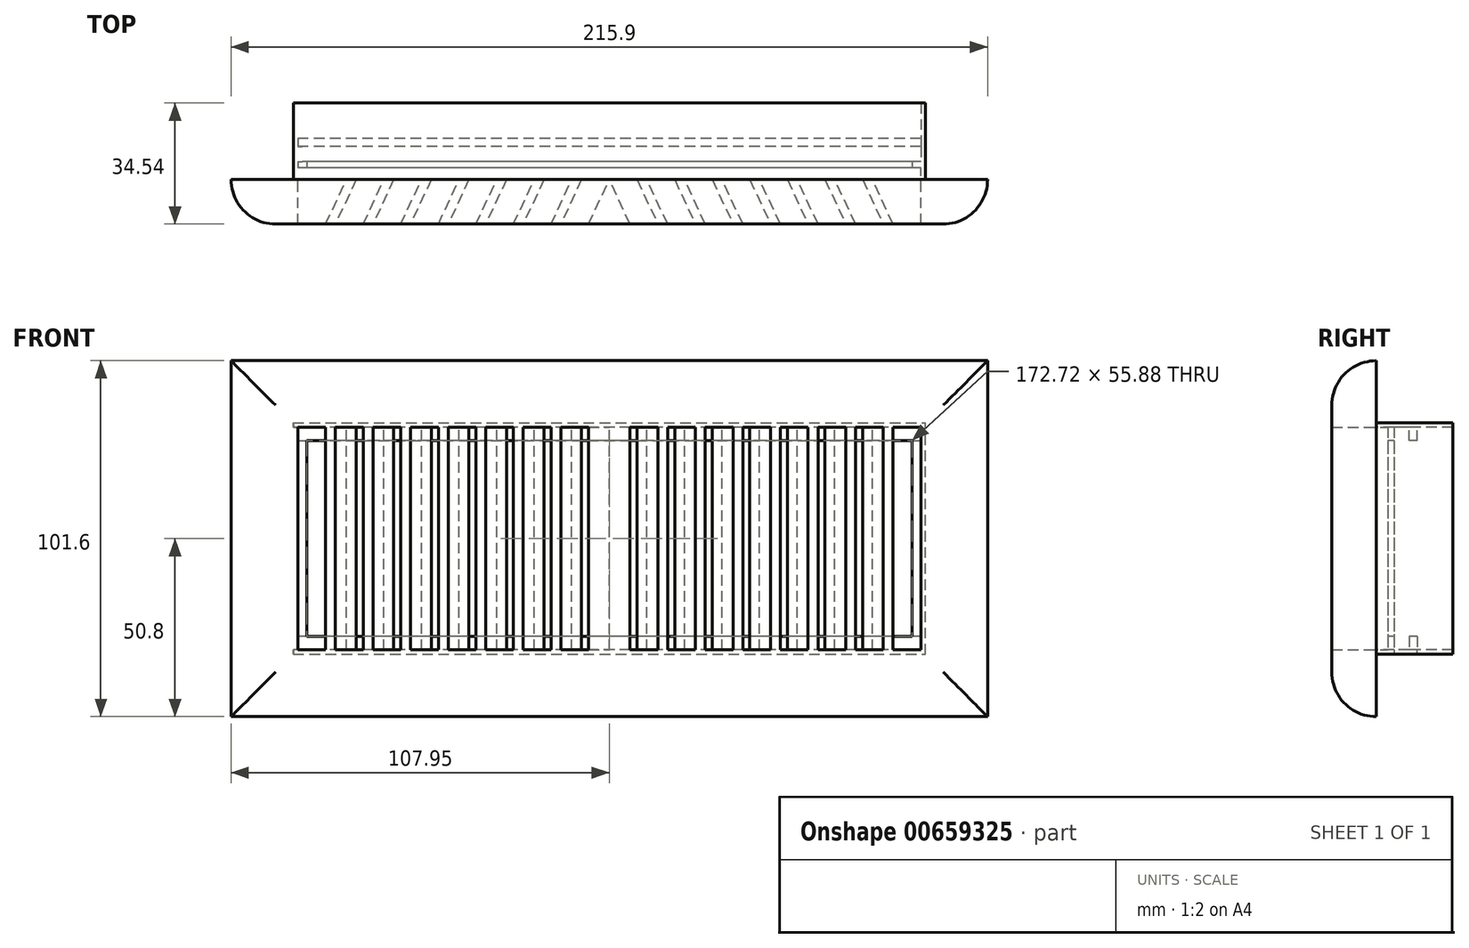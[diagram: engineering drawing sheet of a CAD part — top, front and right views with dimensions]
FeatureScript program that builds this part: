
annotation { "Feature Type Name" : "Feature", "Feature Type Description" : "" }
export const myFeature = defineFeature(function(context is Context, id is Id, definition is map)
    precondition{}
    {
        {
            var Q0;
            Q0=qCreatedBy(makeId("Front.planeOp"),FACE);
            var sketch = newSketch(context, id + "F0", { "sketchPlane" : qUnion([Q0])});
            skLineSegment(sketch, "E0.bottom", {"start": v(107.95, -50.8) * mm, "end": v(-107.95, -50.8) * mm});
            skLineSegment(sketch, "E0.top", {"start": v(107.95, 50.8) * mm, "end": v(-107.95, 50.8) * mm});
            skLineSegment(sketch, "E0.left", {"start": v(107.95, -50.8) * mm, "end": v(107.95, 50.8) * mm});
            skLineSegment(sketch, "E0.right", {"start": v(-107.95, -50.8) * mm, "end": v(-107.95, 50.8) * mm});
            skPoint(sketch, "E0.middle", {"position": v(0, 0) * mm});
            skLineSegment(sketch, "E1.bottom", {"start": v(88.9, -31.75) * mm, "end": v(-88.9, -31.75) * mm});
            skLineSegment(sketch, "E1.top", {"start": v(88.9, 31.75) * mm, "end": v(-88.9, 31.75) * mm});
            skLineSegment(sketch, "E1.left", {"start": v(88.9, -31.75) * mm, "end": v(88.9, 31.75) * mm});
            skLineSegment(sketch, "E1.right", {"start": v(-88.9, -31.75) * mm, "end": v(-88.9, 31.75) * mm});
            skSolve(sketch);
        }
        {
            var Q0;
            Q0=makeQuery(id+"F0.imprint","IMPRINT",FACE,{"disambiguationData":[TD([[makeQuery(id+"F0.imprint","IMPRINT",EDGE,{"derivedFrom":sQuery(id+"F0.wireOp",EDGE,"E0.bottom")}),-1.0]])]});
            extrude(context, id + "F1", {"entities" : qUnion([Q0]), "depth" : 12.7 * mm});
        }
        {
            var Q0;
            Q0=makeQuery(id+"F1.opExtrude","SWEPT_FACE",FACE,{"disambiguationData":[OSD([sQuery(id+"F0.wireOp",EDGE,"E0.top")])]});
            var sketch = newSketch(context, id + "F2", { "sketchPlane" : qUnion([Q0])});
            skLineSegment(sketch, "E2", {"start": v(-75.05, 0) * mm, "end": v(-80.97, -12.7) * mm});
            skLineSegment(sketch, "E3", {"start": v(-80.97, -12.7) * mm, "end": v(-78.17, -12.7) * mm});
            skLineSegment(sketch, "E4", {"start": v(-78.17, -12.7) * mm, "end": v(-72.25, 0) * mm});
            skLineSegment(sketch, "E5", {"start": v(-72.25, 0) * mm, "end": v(-75.05, 0) * mm});
            skLineSegment(sketch, "E6.1.0.0", {"start": v(-64.33, 0) * mm, "end": v(-70.25, -12.7) * mm});
            skLineSegment(sketch, "E6.1.0.1", {"start": v(-70.25, -12.7) * mm, "end": v(-67.45, -12.7) * mm});
            skLineSegment(sketch, "E6.1.0.2", {"start": v(-67.45, -12.7) * mm, "end": v(-61.53, 0) * mm});
            skLineSegment(sketch, "E6.1.0.3", {"start": v(-61.53, 0) * mm, "end": v(-64.33, 0) * mm});
            skLineSegment(sketch, "E6.2.0.0", {"start": v(-53.6, 0) * mm, "end": v(-59.53, -12.7) * mm});
            skLineSegment(sketch, "E6.2.0.1", {"start": v(-59.53, -12.7) * mm, "end": v(-56.73, -12.7) * mm});
            skLineSegment(sketch, "E6.2.0.2", {"start": v(-56.73, -12.7) * mm, "end": v(-50.8, 0) * mm});
            skLineSegment(sketch, "E6.2.0.3", {"start": v(-50.8, 0) * mm, "end": v(-53.6, 0) * mm});
            skLineSegment(sketch, "E6.3.0.0", {"start": v(-42.88, 0) * mm, "end": v(-48.8, -12.7) * mm});
            skLineSegment(sketch, "E6.3.0.1", {"start": v(-48.8, -12.7) * mm, "end": v(-46, -12.7) * mm});
            skLineSegment(sketch, "E6.3.0.2", {"start": v(-46, -12.7) * mm, "end": v(-40.08, 0) * mm});
            skLineSegment(sketch, "E6.3.0.3", {"start": v(-40.08, 0) * mm, "end": v(-42.88, 0) * mm});
            skLineSegment(sketch, "E6.4.0.0", {"start": v(-32.16, 0) * mm, "end": v(-38.08, -12.7) * mm});
            skLineSegment(sketch, "E6.4.0.1", {"start": v(-38.08, -12.7) * mm, "end": v(-35.28, -12.7) * mm});
            skLineSegment(sketch, "E6.4.0.2", {"start": v(-35.28, -12.7) * mm, "end": v(-29.36, 0) * mm});
            skLineSegment(sketch, "E6.4.0.3", {"start": v(-29.36, 0) * mm, "end": v(-32.16, 0) * mm});
            skLineSegment(sketch, "E6.5.0.0", {"start": v(-21.44, 0) * mm, "end": v(-27.36, -12.7) * mm});
            skLineSegment(sketch, "E6.5.0.1", {"start": v(-27.36, -12.7) * mm, "end": v(-24.56, -12.7) * mm});
            skLineSegment(sketch, "E6.5.0.2", {"start": v(-24.56, -12.7) * mm, "end": v(-18.64, 0) * mm});
            skLineSegment(sketch, "E6.5.0.3", {"start": v(-18.64, 0) * mm, "end": v(-21.44, 0) * mm});
            skLineSegment(sketch, "E6.6.0.0", {"start": v(-10.72, 0) * mm, "end": v(-16.64, -12.7) * mm});
            skLineSegment(sketch, "E6.6.0.1", {"start": v(-16.64, -12.7) * mm, "end": v(-13.84, -12.7) * mm});
            skLineSegment(sketch, "E6.6.0.2", {"start": v(-13.84, -12.7) * mm, "end": v(-7.92, 0) * mm});
            skLineSegment(sketch, "E6.6.0.3", {"start": v(-7.92, 0) * mm, "end": v(-10.72, 0) * mm});
            skLineSegment(sketch, "E6.direction1", {"start": v(-80.97, -12.7) * mm, "end": v(-70.25, -12.7) * mm, "construction": true});
            skLineSegment(sketch, "E7", {"start": v(75.05, 0) * mm, "end": v(80.97, -12.7) * mm});
            skLineSegment(sketch, "E8", {"start": v(80.97, -12.7) * mm, "end": v(78.17, -12.7) * mm});
            skLineSegment(sketch, "E9", {"start": v(78.17, -12.7) * mm, "end": v(72.25, 0) * mm});
            skLineSegment(sketch, "E10", {"start": v(72.25, 0) * mm, "end": v(75.05, 0) * mm});
            skLineSegment(sketch, "E11.1.0.0", {"start": v(70.25, -12.7) * mm, "end": v(67.45, -12.7) * mm});
            skLineSegment(sketch, "E11.1.0.1", {"start": v(64.33, 0) * mm, "end": v(70.25, -12.7) * mm});
            skLineSegment(sketch, "E11.1.0.2", {"start": v(61.53, 0) * mm, "end": v(64.33, 0) * mm});
            skLineSegment(sketch, "E11.1.0.3", {"start": v(67.45, -12.7) * mm, "end": v(61.53, 0) * mm});
            skLineSegment(sketch, "E11.2.0.0", {"start": v(59.53, -12.7) * mm, "end": v(56.73, -12.7) * mm});
            skLineSegment(sketch, "E11.2.0.1", {"start": v(53.6, 0) * mm, "end": v(59.53, -12.7) * mm});
            skLineSegment(sketch, "E11.2.0.2", {"start": v(50.8, 0) * mm, "end": v(53.6, 0) * mm});
            skLineSegment(sketch, "E11.2.0.3", {"start": v(56.73, -12.7) * mm, "end": v(50.8, 0) * mm});
            skLineSegment(sketch, "E11.3.0.0", {"start": v(48.8, -12.7) * mm, "end": v(46, -12.7) * mm});
            skLineSegment(sketch, "E11.3.0.1", {"start": v(42.88, 0) * mm, "end": v(48.8, -12.7) * mm});
            skLineSegment(sketch, "E11.3.0.2", {"start": v(40.08, 0) * mm, "end": v(42.88, 0) * mm});
            skLineSegment(sketch, "E11.3.0.3", {"start": v(46, -12.7) * mm, "end": v(40.08, 0) * mm});
            skLineSegment(sketch, "E11.4.0.0", {"start": v(38.08, -12.7) * mm, "end": v(35.28, -12.7) * mm});
            skLineSegment(sketch, "E11.4.0.1", {"start": v(32.16, 0) * mm, "end": v(38.08, -12.7) * mm});
            skLineSegment(sketch, "E11.4.0.2", {"start": v(29.36, 0) * mm, "end": v(32.16, 0) * mm});
            skLineSegment(sketch, "E11.4.0.3", {"start": v(35.28, -12.7) * mm, "end": v(29.36, 0) * mm});
            skLineSegment(sketch, "E11.5.0.0", {"start": v(27.36, -12.7) * mm, "end": v(24.56, -12.7) * mm});
            skLineSegment(sketch, "E11.5.0.1", {"start": v(21.44, 0) * mm, "end": v(27.36, -12.7) * mm});
            skLineSegment(sketch, "E11.5.0.2", {"start": v(18.64, 0) * mm, "end": v(21.44, 0) * mm});
            skLineSegment(sketch, "E11.5.0.3", {"start": v(24.56, -12.7) * mm, "end": v(18.64, 0) * mm});
            skLineSegment(sketch, "E11.6.0.0", {"start": v(16.64, -12.7) * mm, "end": v(13.84, -12.7) * mm});
            skLineSegment(sketch, "E11.6.0.1", {"start": v(10.72, 0) * mm, "end": v(16.64, -12.7) * mm});
            skLineSegment(sketch, "E11.6.0.2", {"start": v(7.92, 0) * mm, "end": v(10.72, 0) * mm});
            skLineSegment(sketch, "E11.6.0.3", {"start": v(13.84, -12.7) * mm, "end": v(7.92, 0) * mm});
            skLineSegment(sketch, "E11.direction1", {"start": v(78.17, -12.7) * mm, "end": v(67.45, -12.7) * mm, "construction": true});
            skLineSegment(sketch, "E12", {"start": v(0, 0) * mm, "end": v(0, -12.7) * mm, "construction": true});
            skLineSegment(sketch, "E13", {"start": v(0, 0) * mm, "end": v(-5.92, -12.7) * mm});
            skLineSegment(sketch, "E14", {"start": v(0, 0) * mm, "end": v(5.92, -12.7) * mm});
            skLineSegment(sketch, "E15", {"start": v(-5.92, -12.7) * mm, "end": v(5.92, -12.7) * mm});
            skSolve(sketch);
        }
        {
            var Q0;
            Q0=qSketchRegion(id+"F2",true);
            extrude(context, id + "F3", {"entities" : qUnion([Q0]), "operationType" : NewBodyOperationType.ADD, "oppositeDirection" : true, "depth" : 101.6 * mm});
        }
        {
            var Q0;
            Q0=makeQuery(id+"F1.opExtrude","CAP_EDGE",EDGE,{"disambiguationData":[OSD([sQuery(id+"F0.wireOp",EDGE,"E0.top")])],"isStart":false});
            var Q1;
            Q1=makeQuery(id+"F1.opExtrude","CAP_EDGE",EDGE,{"disambiguationData":[OSD([sQuery(id+"F0.wireOp",EDGE,"E0.right")])],"isStart":false});
            var Q2;
            Q2=makeQuery(id+"F1.opExtrude","CAP_EDGE",EDGE,{"disambiguationData":[OSD([sQuery(id+"F0.wireOp",EDGE,"E0.bottom")])],"isStart":false});
            var Q3;
            Q3=makeQuery(id+"F1.opExtrude","CAP_EDGE",EDGE,{"disambiguationData":[OSD([sQuery(id+"F0.wireOp",EDGE,"E0.left")])],"isStart":false});
            fillet(context, id + "F4", {"entities" : qUnion([Q0, Q1, Q2, Q3]), "radius" : 12.7 * mm, "tangentPropagation" : true, "allowEdgeOverflow" : false});
        }
        {
            var Q0;
            Q0=makeQuery(id+"F3.boolean.opBoolean","MERGE",FACE,{"derivedFrom":[makeQuery(id+"F1.opExtrude","CAP_FACE",FACE,{"disambiguationData":[OSD([sQuery(id+"F0.wireOp",EDGE,"E0.bottom"),sQuery(id+"F0.wireOp",EDGE,"E0.top"),sQuery(id+"F0.wireOp",EDGE,"E0.left"),sQuery(id+"F0.wireOp",EDGE,"E0.right"),sQuery(id+"F0.wireOp",EDGE,"E1.bottom"),sQuery(id+"F0.wireOp",EDGE,"E1.top"),sQuery(id+"F0.wireOp",EDGE,"E1.left"),sQuery(id+"F0.wireOp",EDGE,"E1.right")])],"isStart":true}),makeQuery(id+"F3.opExtrude","SWEPT_FACE",FACE,{"disambiguationData":[OSD([sQuery(id+"F2.wireOp",EDGE,"E5")])]}),makeQuery(id+"F3.opExtrude","SWEPT_FACE",FACE,{"disambiguationData":[OSD([sQuery(id+"F2.wireOp",EDGE,"E6.1.0.3")])]}),makeQuery(id+"F3.opExtrude","SWEPT_FACE",FACE,{"disambiguationData":[OSD([sQuery(id+"F2.wireOp",EDGE,"E6.2.0.3")])]}),makeQuery(id+"F3.opExtrude","SWEPT_FACE",FACE,{"disambiguationData":[OSD([sQuery(id+"F2.wireOp",EDGE,"E6.3.0.3")])]}),makeQuery(id+"F3.opExtrude","SWEPT_FACE",FACE,{"disambiguationData":[OSD([sQuery(id+"F2.wireOp",EDGE,"E6.4.0.3")])]}),makeQuery(id+"F3.opExtrude","SWEPT_FACE",FACE,{"disambiguationData":[OSD([sQuery(id+"F2.wireOp",EDGE,"E6.5.0.3")])]}),makeQuery(id+"F3.opExtrude","SWEPT_FACE",FACE,{"disambiguationData":[OSD([sQuery(id+"F2.wireOp",EDGE,"E6.6.0.3")])]}),makeQuery(id+"F3.opExtrude","SWEPT_FACE",FACE,{"disambiguationData":[OSD([sQuery(id+"F2.wireOp",EDGE,"E10")])]}),makeQuery(id+"F3.opExtrude","SWEPT_FACE",FACE,{"disambiguationData":[OSD([sQuery(id+"F2.wireOp",EDGE,"E11.1.0.2")])]}),makeQuery(id+"F3.opExtrude","SWEPT_FACE",FACE,{"disambiguationData":[OSD([sQuery(id+"F2.wireOp",EDGE,"E11.2.0.2")])]}),makeQuery(id+"F3.opExtrude","SWEPT_FACE",FACE,{"disambiguationData":[OSD([sQuery(id+"F2.wireOp",EDGE,"E11.3.0.2")])]}),makeQuery(id+"F3.opExtrude","SWEPT_FACE",FACE,{"disambiguationData":[OSD([sQuery(id+"F2.wireOp",EDGE,"E11.4.0.2")])]}),makeQuery(id+"F3.opExtrude","SWEPT_FACE",FACE,{"disambiguationData":[OSD([sQuery(id+"F2.wireOp",EDGE,"E11.5.0.2")])]}),makeQuery(id+"F3.opExtrude","SWEPT_FACE",FACE,{"disambiguationData":[OSD([sQuery(id+"F2.wireOp",EDGE,"E11.6.0.2")])]})]});
            var sketch = newSketch(context, id + "F5", { "sketchPlane" : qUnion([Q0])});
            skLineSegment(sketch, "E16.bottom", {"start": v(90.17, -33.02) * mm, "end": v(-90.17, -33.02) * mm});
            skLineSegment(sketch, "E16.top", {"start": v(90.17, 33.02) * mm, "end": v(-90.17, 33.02) * mm});
            skLineSegment(sketch, "E16.right", {"start": v(-90.17, -33.02) * mm, "end": v(-90.17, 33.02) * mm});
            skPoint(sketch, "E16.middle", {"position": v(0, 0) * mm});
            skLineSegment(sketch, "E17.bottom", {"start": v(88.9, -31.75) * mm, "end": v(-88.9, -31.75) * mm});
            skLineSegment(sketch, "E17.top", {"start": v(88.9, 31.75) * mm, "end": v(-88.9, 31.75) * mm});
            skLineSegment(sketch, "E17.right", {"start": v(-88.9, -31.75) * mm, "end": v(-88.9, 31.75) * mm});
            skLineSegment(sketch, "E18", {"start": v(88.9, 31.75) * mm, "end": v(90.17, 31.75) * mm});
            skLineSegment(sketch, "E19", {"start": v(90.17, 31.75) * mm, "end": v(90.17, 33.02) * mm});
            skLineSegment(sketch, "E20", {"start": v(88.9, -31.75) * mm, "end": v(90.17, -31.75) * mm});
            skLineSegment(sketch, "E21", {"start": v(90.17, -31.75) * mm, "end": v(90.17, -33.02) * mm});
            skSolve(sketch);
        }
        {
            var Q0;
            Q0=qSketchRegion(id+"F5",true);
            extrude(context, id + "F6", {"entities" : qUnion([Q0]), "operationType" : NewBodyOperationType.ADD, "depth" : 3.3 * mm});
        }
        {
            var Q0;
            Q0=makeQuery(id+"F6.opExtrude","CAP_FACE",FACE,{"disambiguationData":[OSD([sQuery(id+"F5.wireOp",EDGE,"E16.bottom"),sQuery(id+"F5.wireOp",EDGE,"E16.top"),sQuery(id+"F5.wireOp",EDGE,"E16.right"),sQuery(id+"F5.wireOp",EDGE,"E17.bottom"),sQuery(id+"F5.wireOp",EDGE,"E17.top"),sQuery(id+"F5.wireOp",EDGE,"E17.right"),sQuery(id+"F5.wireOp",EDGE,"E18"),sQuery(id+"F5.wireOp",EDGE,"E19"),sQuery(id+"F5.wireOp",EDGE,"E20"),sQuery(id+"F5.wireOp",EDGE,"E21")])],"isStart":false});
            var sketch = newSketch(context, id + "F7", { "sketchPlane" : qUnion([Q0])});
            skLineSegment(sketch, "E22.bottom", {"start": v(-90.17, 33.02) * mm, "end": v(88.9, 33.02) * mm});
            skLineSegment(sketch, "E22.top", {"start": v(-90.17, -33.02) * mm, "end": v(88.9, -33.02) * mm});
            skLineSegment(sketch, "E22.left", {"start": v(-90.17, 33.02) * mm, "end": v(-90.17, -33.02) * mm});
            skLineSegment(sketch, "E22.right", {"start": v(88.9, 33.02) * mm, "end": v(88.9, -33.02) * mm});
            skLineSegment(sketch, "E23.bottom", {"start": v(-86.36, 27.94) * mm, "end": v(86.36, 27.94) * mm});
            skLineSegment(sketch, "E23.top", {"start": v(-86.36, -27.94) * mm, "end": v(86.36, -27.94) * mm});
            skLineSegment(sketch, "E23.left", {"start": v(-86.36, 27.94) * mm, "end": v(-86.36, -27.94) * mm});
            skLineSegment(sketch, "E23.right", {"start": v(86.36, 27.94) * mm, "end": v(86.36, -27.94) * mm});
            skSolve(sketch);
        }
        {
            var Q0;
            Q0=qSketchRegion(id+"F7",true);
            extrude(context, id + "F8", {"entities" : qUnion([Q0]), "operationType" : NewBodyOperationType.ADD, "depth" : 1.78 * mm});
        }
        {
            var Q0;
            Q0=makeQuery(id+"F8.opExtrude","CAP_FACE",FACE,{"disambiguationData":[OSD([sQuery(id+"F7.wireOp",EDGE,"E22.bottom"),sQuery(id+"F7.wireOp",EDGE,"E22.top"),sQuery(id+"F7.wireOp",EDGE,"E22.left"),sQuery(id+"F7.wireOp",EDGE,"E22.right"),sQuery(id+"F7.wireOp",EDGE,"E23.bottom"),sQuery(id+"F7.wireOp",EDGE,"E23.top"),sQuery(id+"F7.wireOp",EDGE,"E23.left"),sQuery(id+"F7.wireOp",EDGE,"E23.right")])],"isStart":false});
            var sketch = newSketch(context, id + "F9", { "sketchPlane" : qUnion([Q0])});
            skLineSegment(sketch, "E24.bottom", {"start": v(-90.17, 33.02) * mm, "end": v(88.9, 33.02) * mm});
            skLineSegment(sketch, "E24.top", {"start": v(-90.17, -33.02) * mm, "end": v(88.9, -33.02) * mm});
            skLineSegment(sketch, "E24.left", {"start": v(-90.17, 33.02) * mm, "end": v(-90.17, -33.02) * mm});
            skLineSegment(sketch, "E25.bottom", {"start": v(-88.9, 31.75) * mm, "end": v(87.63, 31.75) * mm});
            skLineSegment(sketch, "E25.top", {"start": v(-88.9, -31.75) * mm, "end": v(87.63, -31.75) * mm});
            skLineSegment(sketch, "E25.left", {"start": v(-88.9, 31.75) * mm, "end": v(-88.9, -31.75) * mm});
            skLineSegment(sketch, "E26", {"start": v(88.9, -33.02) * mm, "end": v(90.18, -33.02) * mm});
            skLineSegment(sketch, "E27", {"start": v(90.18, -33.02) * mm, "end": v(90.18, -31.75) * mm});
            skLineSegment(sketch, "E28", {"start": v(90.18, -31.75) * mm, "end": v(87.63, -31.75) * mm});
            skLineSegment(sketch, "E29", {"start": v(88.9, 33.02) * mm, "end": v(90.17, 33.02) * mm});
            skLineSegment(sketch, "E30", {"start": v(90.17, 33.02) * mm, "end": v(90.17, 31.75) * mm});
            skLineSegment(sketch, "E31", {"start": v(90.17, 31.75) * mm, "end": v(87.63, 31.75) * mm});
            skSolve(sketch);
        }
        {
            var Q0;
            {var subQ5=sQuery(id+"F9.wireOp",EDGE,"E24.bottom");Q0=makeQuery(id+"F9.imprint","IMPRINT",FACE,{"disambiguationData":[TD([[makeQuery(id+"F9.imprint","IMPRINT",EDGE,{"derivedFrom":subQ5}),1.0]])]});}
            var Q1;
            {var subQ0=sQuery(id+"F9.wireOp",EDGE,"E29");Q1=makeQuery(id+"F9.imprint","IMPRINT",FACE,{"disambiguationData":[TD([[makeQuery(id+"F9.imprint","IMPRINT",EDGE,{"derivedFrom":subQ0}),-1.0]])]});}
            var Q2;
            {var subQ0=sQuery(id+"F9.wireOp",EDGE,"E26");Q2=makeQuery(id+"F9.imprint","IMPRINT",FACE,{"disambiguationData":[TD([[makeQuery(id+"F9.imprint","IMPRINT",EDGE,{"derivedFrom":subQ0}),1.0]])]});}
            extrude(context, id + "F10", {"entities" : qUnion([Q0, Q1, Q2]), "operationType" : NewBodyOperationType.ADD, "depth" : 4.32 * mm});
        }
        {
            var Q0;
            {var subQ0=sQuery(id+"F5.wireOp",EDGE,"E21");var subQ1=sQuery(id+"F5.wireOp",EDGE,"E20");var subQ2=sQuery(id+"F5.wireOp",EDGE,"E17.bottom");var subQ3=sQuery(id+"F5.wireOp",EDGE,"E16.bottom");Q0=makeQuery(id+"F8.boolean.opBoolean","SPLIT",FACE,{"disambiguationData":[TD([makeQuery(id+"F1.opExtrude","SWEPT_FACE",FACE,{"disambiguationData":[OSD([sQuery(id+"F0.wireOp",EDGE,"E1.bottom")])]})])],"derivedFrom":makeQuery(id+"F6.opExtrude","CAP_FACE",FACE,{"disambiguationData":[OSD([subQ3,sQuery(id+"F5.wireOp",EDGE,"E16.top"),sQuery(id+"F5.wireOp",EDGE,"E16.right"),subQ2,sQuery(id+"F5.wireOp",EDGE,"E17.top"),sQuery(id+"F5.wireOp",EDGE,"E17.right"),sQuery(id+"F5.wireOp",EDGE,"E18"),sQuery(id+"F5.wireOp",EDGE,"E19"),subQ1,subQ0])],"isStart":false})});}
            var sketch = newSketch(context, id + "F11", { "sketchPlane" : qUnion([Q0])});
            skLineSegment(sketch, "E32.bottom", {"start": v(88.9, -33.02) * mm, "end": v(90.17, -33.02) * mm});
            skLineSegment(sketch, "E32.top", {"start": v(88.9, -31.75) * mm, "end": v(90.17, -31.75) * mm});
            skLineSegment(sketch, "E32.left", {"start": v(88.9, -33.02) * mm, "end": v(88.9, -31.75) * mm});
            skLineSegment(sketch, "E32.right", {"start": v(90.17, -33.02) * mm, "end": v(90.17, -31.75) * mm});
            skSolve(sketch);
        }
        {
            var Q0;
            Q0=qSketchRegion(id+"F11",true);
            extrude(context, id + "F12", {"entities" : qUnion([Q0]), "operationType" : NewBodyOperationType.ADD, "depth" : 1.78 * mm});
        }
        {
            var Q0;
            Q0=makeQuery(id+"F10.opExtrude","CAP_FACE",FACE,{"disambiguationData":[OSD([sQuery(id+"F9.wireOp",EDGE,"E24.bottom"),sQuery(id+"F9.wireOp",EDGE,"E24.top"),sQuery(id+"F9.wireOp",EDGE,"E24.left"),sQuery(id+"F9.wireOp",EDGE,"E25.bottom"),sQuery(id+"F9.wireOp",EDGE,"E25.top"),sQuery(id+"F9.wireOp",EDGE,"E25.left"),sQuery(id+"F9.wireOp",EDGE,"E26"),sQuery(id+"F9.wireOp",EDGE,"E27"),sQuery(id+"F9.wireOp",EDGE,"E28"),sQuery(id+"F9.wireOp",EDGE,"E29"),sQuery(id+"F9.wireOp",EDGE,"E30"),sQuery(id+"F9.wireOp",EDGE,"E31")])],"isStart":false});
            var sketch = newSketch(context, id + "F13", { "sketchPlane" : qUnion([Q0])});
            skLineSegment(sketch, "E33.bottom", {"start": v(-90.17, 33.02) * mm, "end": v(88.9, 33.02) * mm});
            skLineSegment(sketch, "E33.top", {"start": v(-90.17, -33.02) * mm, "end": v(88.9, -33.02) * mm});
            skLineSegment(sketch, "E34.bottom", {"start": v(-84.84, 27.94) * mm, "end": v(88.9, 27.94) * mm});
            skLineSegment(sketch, "E34.top", {"start": v(-84.84, -27.94) * mm, "end": v(88.9, -27.94) * mm});
            skLineSegment(sketch, "E35", {"start": v(-84.84, 27.94) * mm, "end": v(-90.17, 27.94) * mm});
            skLineSegment(sketch, "E36", {"start": v(-90.17, 27.94) * mm, "end": v(-90.17, 33.02) * mm});
            skLineSegment(sketch, "E37", {"start": v(-84.84, -27.94) * mm, "end": v(-90.17, -27.94) * mm});
            skLineSegment(sketch, "E38", {"start": v(-90.17, -27.94) * mm, "end": v(-90.17, -33.02) * mm});
            skLineSegment(sketch, "E39.bottom", {"start": v(-90.17, 27.94) * mm, "end": v(-88.9, 27.94) * mm});
            skLineSegment(sketch, "E39.top", {"start": v(-90.17, -27.94) * mm, "end": v(-88.9, -27.94) * mm});
            skLineSegment(sketch, "E39.left", {"start": v(-90.17, 27.94) * mm, "end": v(-90.17, -27.94) * mm});
            skLineSegment(sketch, "E39.right", {"start": v(-88.9, 27.94) * mm, "end": v(-88.9, -27.94) * mm});
            skLineSegment(sketch, "E40", {"start": v(88.9, -27.94) * mm, "end": v(88.9, -33.02) * mm});
            skLineSegment(sketch, "E41", {"start": v(88.9, 27.94) * mm, "end": v(88.9, 33.02) * mm});
            skSolve(sketch);
        }
        {
            var Q0;
            Q0=qSketchRegion(id+"F13",true);
            extrude(context, id + "F14", {"entities" : qUnion([Q0]), "operationType" : NewBodyOperationType.ADD, "depth" : 2.3 * mm});
        }
        {
            var Q0;
            Q0=makeQuery(id+"F14.opExtrude","SWEPT_FACE",FACE,{"disambiguationData":[OSD([sQuery(id+"F13.wireOp",EDGE,"E34.top"),sQuery(id+"F13.wireOp",EDGE,"E37"),sQuery(id+"F13.wireOp",EDGE,"TGxW7JvE-hO0u-tt39-ioUT-bYuH0o1wrKsi")])]});
            var sketch = newSketch(context, id + "F15", { "sketchPlane" : qUnion([Q0])});
            skSolve(sketch);
        }
        {
            var Q0;
            Q0=makeQuery(id+"Fv8F5Soem3vfvmW_1.boolean.opBoolean","MERGE",FACE,{"derivedFrom":[makeQuery(id+"F14.opExtrude","CAP_FACE",FACE,{"disambiguationData":[OSD([sQuery(id+"F13.wireOp",EDGE,"E33.bottom"),sQuery(id+"F13.wireOp",EDGE,"E33.top"),sQuery(id+"F13.wireOp",EDGE,"E34.bottom"),sQuery(id+"F13.wireOp",EDGE,"E34.top"),sQuery(id+"F13.wireOp",EDGE,"E35"),sQuery(id+"F13.wireOp",EDGE,"E36"),sQuery(id+"F13.wireOp",EDGE,"E37"),sQuery(id+"F13.wireOp",EDGE,"E38"),sQuery(id+"F13.wireOp",EDGE,"E39.left"),sQuery(id+"F13.wireOp",EDGE,"E39.right"),sQuery(id+"F13.wireOp",EDGE,"TGxW7JvE-hO0u-tt39-ioUT-bYuH0o1wrKsi"),sQuery(id+"F13.wireOp",EDGE,"xJwFBrmR-DKHQ-Ms6E-cGLF-1sDl0en4KIHk"),sQuery(id+"F13.wireOp",EDGE,"KjPjYPhn-M9NA-BWyU-6eae-7lh8KEkwCyoe"),sQuery(id+"F13.wireOp",EDGE,"DDPbrne3-7nOW-QVff-d2O1-u6GeuogKL0BI")])],"isStart":false}),makeQuery(id+"Fv8F5Soem3vfvmW_1.opExtrude","SWEPT_FACE",FACE,{"disambiguationData":[OSD([sQuery(id+"F15.wireOp",EDGE,"I5fvG48v-rP8C-mtnB-2jEv-sWBCkAZKz6mY.bottom")])]})]});
            var sketch = newSketch(context, id + "F16", { "sketchPlane" : qUnion([Q0])});
            skLineSegment(sketch, "E42.bottom", {"start": v(-90.17, 33.02) * mm, "end": v(90.17, 33.02) * mm});
            skLineSegment(sketch, "E42.top", {"start": v(-90.17, -33.02) * mm, "end": v(90.17, -33.02) * mm});
            skLineSegment(sketch, "E42.left", {"start": v(-90.17, 33.02) * mm, "end": v(-90.17, -33.02) * mm});
            skLineSegment(sketch, "E43.bottom", {"start": v(-88.9, 31.75) * mm, "end": v(84.62, 31.75) * mm});
            skLineSegment(sketch, "E43.top", {"start": v(-88.9, -31.75) * mm, "end": v(84.62, -31.75) * mm});
            skLineSegment(sketch, "E43.left", {"start": v(-88.9, 31.75) * mm, "end": v(-88.9, -31.75) * mm});
            skLineSegment(sketch, "E44", {"start": v(84.62, 31.75) * mm, "end": v(90.17, 31.75) * mm});
            skLineSegment(sketch, "E45", {"start": v(90.17, 33.02) * mm, "end": v(90.17, 31.75) * mm});
            skLineSegment(sketch, "E46", {"start": v(84.62, -31.75) * mm, "end": v(90.17, -31.75) * mm});
            skLineSegment(sketch, "E47", {"start": v(90.17, -33.02) * mm, "end": v(90.17, -31.75) * mm});
            skSolve(sketch);
        }
        {
            var Q0;
            Q0=qSketchRegion(id+"F16",true);
            extrude(context, id + "F17", {"entities" : qUnion([Q0]), "operationType" : NewBodyOperationType.ADD, "depth" : 10.16 * mm});
        }
        {
            var Q0;
            {var subQ0=sQuery(id+"F5.wireOp",EDGE,"E18");var subQ1=sQuery(id+"F5.wireOp",EDGE,"E17.top");var subQ2=sQuery(id+"F5.wireOp",EDGE,"E19");var subQ3=sQuery(id+"F5.wireOp",EDGE,"E16.top");Q0=makeQuery(id+"F8.boolean.opBoolean","SPLIT",FACE,{"disambiguationData":[TD([makeQuery(id+"F1.opExtrude","SWEPT_FACE",FACE,{"disambiguationData":[OSD([sQuery(id+"F0.wireOp",EDGE,"E1.top")])]})])],"derivedFrom":makeQuery(id+"F6.opExtrude","CAP_FACE",FACE,{"disambiguationData":[OSD([sQuery(id+"F5.wireOp",EDGE,"E16.bottom"),subQ3,sQuery(id+"F5.wireOp",EDGE,"E16.right"),sQuery(id+"F5.wireOp",EDGE,"E17.bottom"),subQ1,sQuery(id+"F5.wireOp",EDGE,"E17.right"),subQ0,subQ2,sQuery(id+"F5.wireOp",EDGE,"E20"),sQuery(id+"F5.wireOp",EDGE,"E21")])],"isStart":false})});}
            var sketch = newSketch(context, id + "F18", { "sketchPlane" : qUnion([Q0])});
            skLineSegment(sketch, "E48.bottom", {"start": v(88.9, 33.02) * mm, "end": v(90.17, 33.02) * mm});
            skLineSegment(sketch, "E48.top", {"start": v(88.9, 31.75) * mm, "end": v(90.17, 31.75) * mm});
            skLineSegment(sketch, "E48.left", {"start": v(88.9, 33.02) * mm, "end": v(88.9, 31.75) * mm});
            skLineSegment(sketch, "E48.right", {"start": v(90.17, 33.02) * mm, "end": v(90.17, 31.75) * mm});
            skSolve(sketch);
        }
        {
            var Q0;
            Q0=qSketchRegion(id+"F18",true);
            extrude(context, id + "F19", {"entities" : qUnion([Q0]), "operationType" : NewBodyOperationType.ADD, "depth" : 1.78 * mm});
        }
        {
            var Q0;
            {var subQ0=sQuery(id+"F9.wireOp",EDGE,"E27");var subQ1=sQuery(id+"F9.wireOp",EDGE,"E26");var subQ2=sQuery(id+"F9.wireOp",EDGE,"E24.top");var subQ4=sQuery(id+"F9.wireOp",EDGE,"E28");Q0=makeQuery(id+"F14.boolean.opBoolean","SPLIT",FACE,{"disambiguationData":[TD([makeQuery(id+"F6.opExtrude","SWEPT_FACE",FACE,{"disambiguationData":[OSD([sQuery(id+"F5.wireOp",EDGE,"E16.bottom")])]})])],"derivedFrom":makeQuery(id+"F10.opExtrude","CAP_FACE",FACE,{"disambiguationData":[OSD([sQuery(id+"F9.wireOp",EDGE,"E24.bottom"),subQ2,sQuery(id+"F9.wireOp",EDGE,"E24.left"),sQuery(id+"F9.wireOp",EDGE,"E25.bottom"),sQuery(id+"F9.wireOp",EDGE,"E25.top"),sQuery(id+"F9.wireOp",EDGE,"E25.left"),subQ1,subQ0,subQ4,sQuery(id+"F9.wireOp",EDGE,"E29"),sQuery(id+"F9.wireOp",EDGE,"E30"),sQuery(id+"F9.wireOp",EDGE,"E31")])],"isStart":false})});}
            var sketch = newSketch(context, id + "F20", { "sketchPlane" : qUnion([Q0])});
            skLineSegment(sketch, "E49.bottom", {"start": v(88.9, -33.02) * mm, "end": v(90.18, -33.02) * mm});
            skLineSegment(sketch, "E49.top", {"start": v(88.9, -31.75) * mm, "end": v(90.18, -31.75) * mm});
            skLineSegment(sketch, "E49.left", {"start": v(88.9, -33.02) * mm, "end": v(88.9, -31.75) * mm});
            skLineSegment(sketch, "E49.right", {"start": v(90.18, -33.02) * mm, "end": v(90.18, -31.75) * mm});
            skSolve(sketch);
        }
        {
            var Q0;
            {var subQ2=sQuery(id+"F9.wireOp",EDGE,"E30");var subQ3=sQuery(id+"F9.wireOp",EDGE,"E29");var subQ4=sQuery(id+"F9.wireOp",EDGE,"E24.bottom");var subQ5=sQuery(id+"F9.wireOp",EDGE,"E31");Q0=makeQuery(id+"F14.boolean.opBoolean","SPLIT",FACE,{"disambiguationData":[TD([makeQuery(id+"F6.opExtrude","SWEPT_FACE",FACE,{"disambiguationData":[OSD([sQuery(id+"F5.wireOp",EDGE,"E16.top")])]})])],"derivedFrom":makeQuery(id+"F10.opExtrude","CAP_FACE",FACE,{"disambiguationData":[OSD([subQ4,sQuery(id+"F9.wireOp",EDGE,"E24.top"),sQuery(id+"F9.wireOp",EDGE,"E24.left"),sQuery(id+"F9.wireOp",EDGE,"E25.bottom"),sQuery(id+"F9.wireOp",EDGE,"E25.top"),sQuery(id+"F9.wireOp",EDGE,"E25.left"),sQuery(id+"F9.wireOp",EDGE,"E26"),sQuery(id+"F9.wireOp",EDGE,"E27"),sQuery(id+"F9.wireOp",EDGE,"E28"),subQ3,subQ2,subQ5])],"isStart":false})});}
            var sketch = newSketch(context, id + "F21", { "sketchPlane" : qUnion([Q0])});
            skLineSegment(sketch, "E50.bottom", {"start": v(88.9, 31.75) * mm, "end": v(90.17, 31.75) * mm});
            skLineSegment(sketch, "E50.top", {"start": v(88.9, 33.02) * mm, "end": v(90.17, 33.02) * mm});
            skLineSegment(sketch, "E50.left", {"start": v(88.9, 31.75) * mm, "end": v(88.9, 33.02) * mm});
            skLineSegment(sketch, "E50.right", {"start": v(90.17, 31.75) * mm, "end": v(90.17, 33.02) * mm});
            skSolve(sketch);
        }
        {
            var Q0;
            Q0=qSketchRegion(id+"F21",true);
            var Q1;
            Q1=qSketchRegion(id+"F20",true);
            extrude(context, id + "F22", {"entities" : qUnion([Q0, Q1]), "operationType" : NewBodyOperationType.ADD, "depth" : 2.3 * mm});
        }
    });
